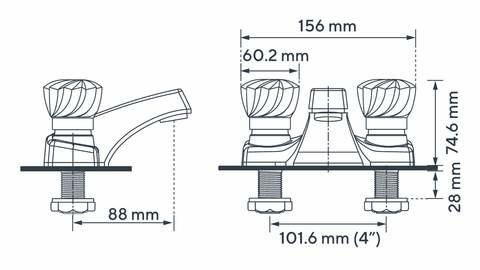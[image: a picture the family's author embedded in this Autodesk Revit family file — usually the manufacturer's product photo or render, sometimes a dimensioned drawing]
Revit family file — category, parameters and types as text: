
# Revit family: 01-1102-00 MEZCLADOR LAVAMANOS 4” KRISTHAL
name_source: partatom
category: Plumbing Fixtures
revit_build: Autodesk Revit 2018 (Build: 20170223_1515(x64)
units: mm (PartAtom-declared; Revit-internal decimal feet)

## family parameters
Cut with Voids When Loaded = No
Host = Face
OmniClass Number = 23.31.11.00
Part Type = Normal
Room Calculation Point = No
Round Connector Dimension = Use Diameter
Shared = No

## types (1)
- 01-1102-00
    Alto = 74.6 mm  [stored 0.244751 ft]
    Ancho = 156 mm  [stored 0.511811 ft]
    CW Connection = Yes
    Default Elevation = 0 mm  [stored 0 ft]
    Description = Bimando baño
    Eje - Rosca = 101.6 mm  [stored 0.333333 ft]
    Eje- Eje = 88 mm  [stored 0.288714 ft]
    HW Connection = Yes
    Link ficha tecnica = https://infotecnica.gricol.com
    Manija = 60.2 mm
    Manufacturer = Gricol
    Model = 01-1102-00
    Plastico ABS Cromado = Plastico - ABS Cromado
    Plastico Acrilico = Plastico Acrilico Transparente
    Product Name = MEZCLADOR LAVAMANOS 4” KRISTHAL
    Type Image = MEZCLADOR LAVAMANOS 4” KRISTHAL.jpg
    URL = https://www.gricol.com
    Vent Connection = No
    Waste Connection = No

note: [stored X ft] marks values corroborated as IEEE doubles in the binary element streams (Revit-internal decimal feet)

## geometry (parser evidence)
native form markers: Blend x4, Sweep x4
no freeform markers — native parametric forms only
